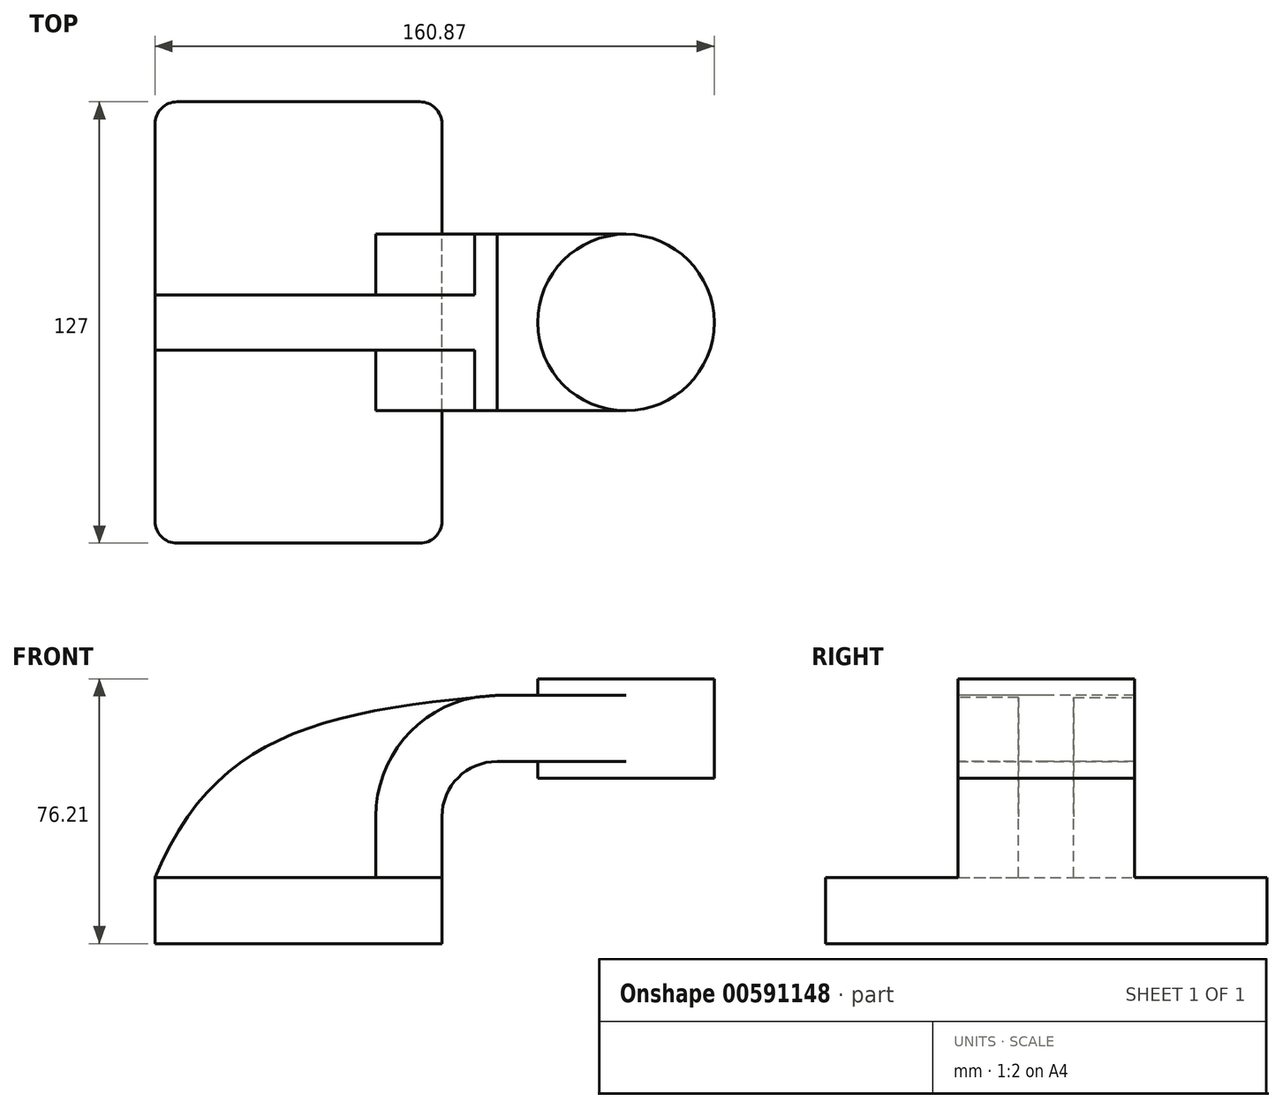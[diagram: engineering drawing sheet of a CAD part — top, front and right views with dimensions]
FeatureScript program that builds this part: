
annotation { "Feature Type Name" : "Feature", "Feature Type Description" : "" }
export const myFeature = defineFeature(function(context is Context, id is Id, definition is map)
    precondition{}
    {
        {
            var Q0;
            Q0=qCreatedBy(makeId("Front.planeOp"),FACE);
            var sketch = newSketch(context, id + "F0", { "sketchPlane" : qUnion([Q0])});
            skLineSegment(sketch, "E0.bottom", {"start": v(41.27, 9.53) * mm, "end": v(-41.28, 9.53) * mm});
            skLineSegment(sketch, "E0.top", {"start": v(41.28, -9.52) * mm, "end": v(-41.27, -9.52) * mm});
            skLineSegment(sketch, "E0.left", {"start": v(41.28, 9.53) * mm, "end": v(41.28, -9.52) * mm});
            skLineSegment(sketch, "E0.right", {"start": v(-41.28, 9.53) * mm, "end": v(-41.28, -9.52) * mm});
            skPoint(sketch, "E0.middle", {"position": v(0, 0) * mm});
            skLineSegment(sketch, "E1.bottom", {"start": v(119.6, 38.1) * mm, "end": v(68.8, 38.1) * mm});
            skLineSegment(sketch, "E1.top", {"start": v(119.6, 66.68) * mm, "end": v(68.8, 66.68) * mm});
            skLineSegment(sketch, "E1.left", {"start": v(119.6, 38.1) * mm, "end": v(119.6, 66.68) * mm});
            skLineSegment(sketch, "E1.right", {"start": v(68.8, 38.1) * mm, "end": v(68.8, 66.68) * mm});
            skPoint(sketch, "E1.middle", {"position": v(94.2, 52.39) * mm});
            skLineSegment(sketch, "E2", {"start": v(41.27, 9.53) * mm, "end": v(41.27, 27) * mm});
            skArc(sketch, "E3", {"start": v(41.27, 27) * mm, "mid": v(45.92, 38.23) * mm, "end": v(57.15, 42.88) * mm});
            skLineSegment(sketch, "E4", {"start": v(57.15, 42.88) * mm, "end": v(94.2, 42.88) * mm});
            skLineSegment(sketch, "E5.0", {"start": v(22.22, 9.53) * mm, "end": v(22.22, 27) * mm});
            skArc(sketch, "E6.0", {"start": v(22.22, 27) * mm, "mid": v(32.45, 51.7) * mm, "end": v(57.15, 61.93) * mm});
            skLineSegment(sketch, "E7.0", {"start": v(57.15, 61.93) * mm, "end": v(94.2, 61.93) * mm});
            skFitSpline(sketch, "E8", {"points": [v(-41.28, 9.53) * mm, v(57.15, 61.93) * mm], "startDerivative": vector(49.67, 120.35) * mm, "endDerivative": vector(158.2, 13.99) * mm});
            skLineSegment(sketch, "E9", {"start": v(94.2, 38.1) * mm, "end": v(94.2, 66.68) * mm});
            skSolve(sketch);
        }
        {
            var Q0;
            Q0=makeQuery(id+"F0.imprint","IMPRINT",FACE,{"disambiguationData":[TD([[makeQuery(id+"F0.imprint","IMPRINT",EDGE,{"derivedFrom":sQuery(id+"F0.wireOp",EDGE,"E0.top")}),-1.0]])]});
            extrude(context, id + "F1", {"entities" : qUnion([Q0]), "endBound" : BoundingType.SYMMETRIC, "depth" : 127 * mm, "offsetDistance" : 25.4 * mm});
        }
        {
            var Q0;
            {var subQ4=sQuery(id+"F0.wireOp",EDGE,"E2");Q0=makeQuery(id+"F0.imprint","IMPRINT",FACE,{"disambiguationData":[TD([[makeQuery(id+"F0.imprint","IMPRINT",EDGE,{"derivedFrom":subQ4}),1.0]])]});}
            var Q1;
            {var subQ5=sQuery(id+"F0.wireOp",EDGE,"IJoRuAZr-t0ju-bvaK-Wltz-ceNwODSlrvHJ");Q1=makeQuery(id+"F0.imprint","IMPRINT",FACE,{"disambiguationData":[TD([[makeQuery(id+"F0.imprint","IMPRINT",EDGE,{"derivedFrom":subQ5}),-1.0]])]});}
            extrude(context, id + "F2", {"entities" : qUnion([Q0, Q1]), "operationType" : NewBodyOperationType.ADD, "endBound" : BoundingType.SYMMETRIC, "depth" : 50.8 * mm, "offsetDistance" : 25.4 * mm});
        }
        {
            var Q0;
            {var subQ3=sQuery(id+"F0.wireOp",EDGE,"E5.0");Q0=makeQuery(id+"F0.imprint","IMPRINT",FACE,{"disambiguationData":[TD([[makeQuery(id+"F0.imprint","IMPRINT",EDGE,{"derivedFrom":subQ3}),1.0]])]});}
            extrude(context, id + "F3", {"entities" : qUnion([Q0]), "operationType" : NewBodyOperationType.ADD, "endBound" : BoundingType.SYMMETRIC, "depth" : 15.88 * mm, "offsetDistance" : 25.4 * mm});
        }
        {
            var Q0;
            {var subQ0=sQuery(id+"F0.wireOp",EDGE,"E4");var subQ1=sQuery(id+"F0.wireOp",EDGE,"E1.right");var subQ2=makeQuery(id+"F0.imprint","INTERSECT",VERTEX,{"derivedFrom":[subQ1,subQ0]});Q0=makeQuery(id+"F0.imprint","IMPRINT",FACE,{"disambiguationData":[TD([[makeQuery(id+"F0.imprint","IMPRINT",EDGE,{"disambiguationData":[TD([[subQ2,-1.0]])],"derivedFrom":subQ1}),-1.0]])]});}
            extrude(context, id + "F4", {"entities" : qUnion([Q0]), "operationType" : NewBodyOperationType.ADD, "endBound" : BoundingType.SYMMETRIC, "depth" : 50.8 * mm, "offsetDistance" : 25.4 * mm});
        }
        {
            var Q0;
            {var subQ4=sQuery(id+"F0.wireOp",EDGE,"E1.left");Q0=makeQuery(id+"F0.imprint","IMPRINT",FACE,{"disambiguationData":[TD([[makeQuery(id+"F0.imprint","IMPRINT",EDGE,{"derivedFrom":subQ4}),1.0]])]});}
            var Q1;
            Q1=sQuery(id+"F0.wireOp",EDGE,"E9");
            revolve(context, id + "F5", {"operationType" : NewBodyOperationType.ADD, "entities" : qUnion([Q0]), "axis" : qUnion([Q1]), "revolveType" : RevolveType.FULL});
        }
        {
            var Q0;
            Q0=makeQuery(id+"F1.opExtrude","CAP_EDGE",EDGE,{"disambiguationData":[OSD([sQuery(id+"F0.wireOp",EDGE,"E0.left")])],"isStart":false});
            var Q1;
            Q1=makeQuery(id+"F1.opExtrude","CAP_EDGE",EDGE,{"disambiguationData":[OSD([sQuery(id+"F0.wireOp",EDGE,"E0.right")])],"isStart":false});
            var Q2;
            Q2=makeQuery(id+"F1.opExtrude","CAP_EDGE",EDGE,{"disambiguationData":[OSD([sQuery(id+"F0.wireOp",EDGE,"E0.left")])],"isStart":true});
            var Q3;
            Q3=makeQuery(id+"F1.opExtrude","CAP_EDGE",EDGE,{"disambiguationData":[OSD([sQuery(id+"F0.wireOp",EDGE,"E0.right")])],"isStart":true});
            fillet(context, id + "F6", {"entities" : qUnion([Q0, Q1, Q2, Q3]), "radius" : 6.35 * mm, "tangentPropagation" : true, "allowEdgeOverflow" : false});
        }
    });
